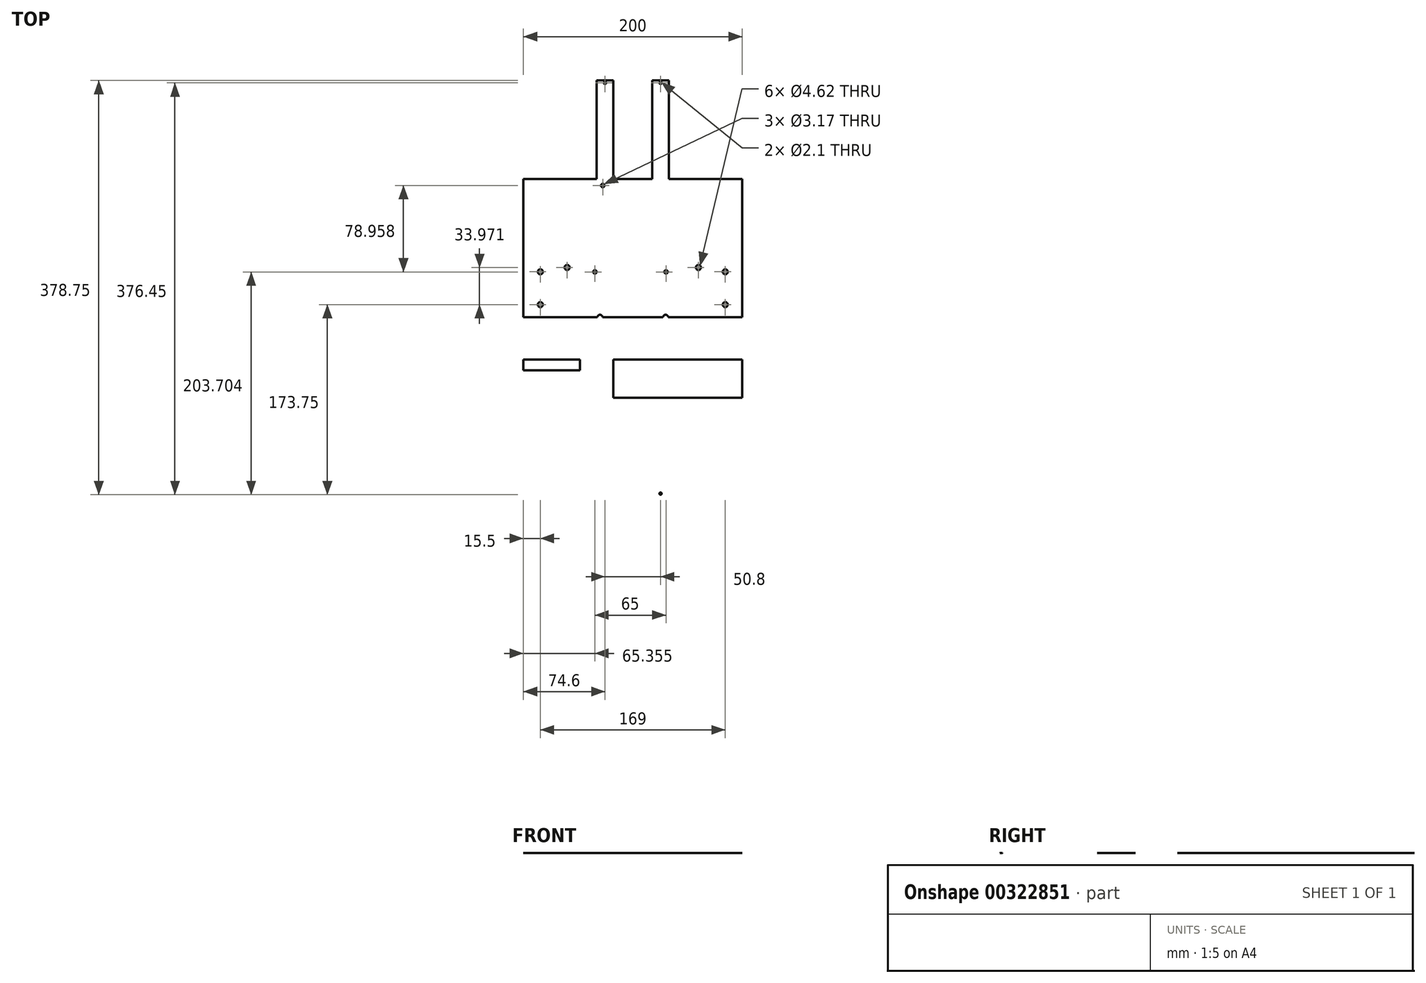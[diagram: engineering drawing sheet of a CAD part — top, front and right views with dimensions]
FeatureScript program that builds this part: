
annotation { "Feature Type Name" : "Feature", "Feature Type Description" : "" }
export const myFeature = defineFeature(function(context is Context, id is Id, definition is map)
    precondition{}
    {
        {
            var Q0;
            Q0=qCreatedBy(makeId("Top.planeOp"),FACE);
            var sketch = newSketch(context, id + "F0", { "sketchPlane" : qUnion([Q0])});
            skLineSegment(sketch, "E0.bottom", {"start": v(100, -100) * mm, "end": v(-100, -100) * mm});
            skLineSegment(sketch, "E0.top", {"start": v(100, 100) * mm, "end": v(-100, 100) * mm});
            skLineSegment(sketch, "E0.left", {"start": v(100, -100) * mm, "end": v(100, 100) * mm});
            skLineSegment(sketch, "E0.right", {"start": v(-100, -100) * mm, "end": v(-100, 100) * mm});
            skPoint(sketch, "E0.middle", {"position": v(0, 0) * mm});
            skLineSegment(sketch, "E1", {"start": v(-100, -100) * mm, "end": v(-100, -65.07) * mm});
            skLineSegment(sketch, "E2", {"start": v(-100, -65.07) * mm, "end": v(100, -65.07) * mm});
            skLineSegment(sketch, "E3", {"start": v(100, -65.07) * mm, "end": v(-100, -65.08) * mm});
            skLineSegment(sketch, "E4", {"start": v(-100, 100) * mm, "end": v(-100, 65.07) * mm});
            skLineSegment(sketch, "E5", {"start": v(-100, 65.07) * mm, "end": v(-42.4, 65.07) * mm});
            skLineSegment(sketch, "E6", {"start": v(100, 65.08) * mm, "end": v(42.4, 65.08) * mm});
            skLineSegment(sketch, "E7", {"start": v(-100, -65.07) * mm, "end": v(-100, -55.08) * mm});
            skLineSegment(sketch, "E8.bottom", {"start": v(-100, -55.08) * mm, "end": v(-48.2, -55.08) * mm});
            skLineSegment(sketch, "E8.top", {"start": v(-100, -75.08) * mm, "end": v(-48.2, -75.08) * mm});
            skLineSegment(sketch, "E8.left", {"start": v(-100, -55.08) * mm, "end": v(-100, -75.08) * mm});
            skLineSegment(sketch, "E8.right", {"start": v(-48.2, -55.08) * mm, "end": v(-48.2, -75.08) * mm});
            skPoint(sketch, "E9.startSnap0", {"position": v(-100, 0) * mm});
            skLineSegment(sketch, "E10.MirrorCS", {"start": v(48.2, -55.08) * mm, "end": v(48.2, -75.08) * mm});
            skLineSegment(sketch, "E11.MirrorCS", {"start": v(100, -75.08) * mm, "end": v(48.2, -75.08) * mm});
            skLineSegment(sketch, "E12.MirrorCS", {"start": v(100, -55.08) * mm, "end": v(48.2, -55.08) * mm});
            skLineSegment(sketch, "E13.MirrorCS", {"start": v(100, 55.08) * mm, "end": v(48.2, 55.08) * mm});
            skLineSegment(sketch, "E14.MirrorCS", {"start": v(48.2, 55.08) * mm, "end": v(48.2, 75.08) * mm});
            skLineSegment(sketch, "E15.MirrorCS", {"start": v(100, 75.08) * mm, "end": v(48.2, 75.08) * mm});
            skLineSegment(sketch, "E16.MirrorCS", {"start": v(-48.2, 55.07) * mm, "end": v(-48.2, 75.07) * mm});
            skLineSegment(sketch, "E17.MirrorCS", {"start": v(-100, 75.07) * mm, "end": v(-48.2, 75.07) * mm});
            skLineSegment(sketch, "E18.MirrorCS", {"start": v(-100, 55.07) * mm, "end": v(-48.2, 55.07) * mm});
            skLineSegment(sketch, "E19.bottom", {"start": v(-100, -55.08) * mm, "end": v(100, -55.08) * mm});
            skLineSegment(sketch, "E19.top", {"start": v(-100, -26.57) * mm, "end": v(100, -26.57) * mm});
            skLineSegment(sketch, "E19.left", {"start": v(-100, -55.08) * mm, "end": v(-100, -26.57) * mm});
            skLineSegment(sketch, "E19.right", {"start": v(100, -55.08) * mm, "end": v(100, -26.57) * mm});
            skLineSegment(sketch, "E20", {"start": v(0, -26.57) * mm, "end": v(30, -26.57) * mm});
            skLineSegment(sketch, "E21", {"start": v(30, -26.57) * mm, "end": v(-30, -26.57) * mm});
            skCircle(sketch, "E22", {"center": v(-30, -26.57) * mm, "radius": 2.31 * mm});
            skCircle(sketch, "E23.MirrorC", {"center": v(30, -26.57) * mm, "radius": 2.31 * mm});
            skLineSegment(sketch, "E24", {"start": v(0, 100) * mm, "end": v(42.4, 100) * mm});
            skLineSegment(sketch, "E25.bottom", {"start": v(42.4, 100) * mm, "end": v(-42.4, 100) * mm});
            skLineSegment(sketch, "E25.top", {"start": v(42.4, 9.75) * mm, "end": v(-42.4, 9.75) * mm});
            skLineSegment(sketch, "E25.left", {"start": v(42.4, 100) * mm, "end": v(42.4, 9.75) * mm});
            skLineSegment(sketch, "E25.right", {"start": v(-42.4, 100) * mm, "end": v(-42.4, 9.75) * mm});
            skPoint(sketch, "E26.start.orphan", {"position": v(0, 18.97) * mm});
            skPoint(sketch, "E27.orphan", {"position": v(-14.32, 0) * mm});
            skLineSegment(sketch, "E28", {"start": v(42.4, 18.97) * mm, "end": v(60, 18.97) * mm});
            skLineSegment(sketch, "E29", {"start": v(60, 18.97) * mm, "end": v(57.69, 18.97) * mm});
            skLineSegment(sketch, "E30", {"start": v(-57.69, 18.97) * mm, "end": v(-60, 18.97) * mm});
            skCircle(sketch, "E31", {"center": v(-60, 18.97) * mm, "radius": 2.31 * mm});
            skCircle(sketch, "E32", {"center": v(60, 18.97) * mm, "radius": 2.31 * mm});
            skLineSegment(sketch, "E33", {"start": v(42.4, 9.75) * mm, "end": v(30.36, 9.75) * mm});
            skLineSegment(sketch, "E34", {"start": v(30.36, 9.75) * mm, "end": v(30.36, 14.95) * mm});
            skCircle(sketch, "E35", {"center": v(30.36, 14.95) * mm, "radius": 1.59 * mm});
            skLineSegment(sketch, "E36", {"start": v(30.36, 14.95) * mm, "end": v(28.77, 14.95) * mm});
            skCircle(sketch, "E37", {"center": v(-34.64, 14.95) * mm, "radius": 1.59 * mm});
            skLineSegment(sketch, "E38", {"start": v(-34.64, 14.95) * mm, "end": v(-27.46, 14.95) * mm});
            skLineSegment(sketch, "E39", {"start": v(-27.46, 92.32) * mm, "end": v(-27.46, 100) * mm});
            skLineSegment(sketch, "E40", {"start": v(-27.46, 100) * mm, "end": v(-27.46, 93.91) * mm});
            skCircle(sketch, "E41", {"center": v(-27.46, 93.91) * mm, "radius": 1.59 * mm});
            skLineSegment(sketch, "E42.trimOffspring", {"start": v(-27.46, 14.95) * mm, "end": v(-34.64, 14.95) * mm});
            skLineSegment(sketch, "E43.trimOffspring", {"start": v(-27.46, 65.07) * mm, "end": v(-42.4, 65.07) * mm});
            skLineSegment(sketch, "E44.trimOffspring", {"start": v(42.4, 65.08) * mm, "end": v(100, 65.08) * mm});
            skLineSegment(sketch, "E45", {"start": v(-100, 0) * mm, "end": v(-84.5, 0) * mm});
            skLineSegment(sketch, "E46", {"start": v(-84.5, 0) * mm, "end": v(-84.5, 15) * mm});
            skLineSegment(sketch, "E47", {"start": v(-84.5, 15) * mm, "end": v(-84.5, -15) * mm});
            skPoint(sketch, "E47.endSnap0", {"position": v(-84.5, 7.5) * mm});
            skCircle(sketch, "E48", {"center": v(-84.5, -15) * mm, "radius": 2.31 * mm});
            skCircle(sketch, "E49", {"center": v(-84.5, 15) * mm, "radius": 2.31 * mm});
            skLineSegment(sketch, "E50", {"start": v(0, -26.57) * mm, "end": v(0, -10.45) * mm});
            skCircle(sketch, "E51.MirrorC", {"center": v(84.5, -15) * mm, "radius": 2.31 * mm});
            skCircle(sketch, "E52.MirrorC", {"center": v(84.5, 15) * mm, "radius": 2.31 * mm});
            skLineSegment(sketch, "E53.left", {"start": v(33.02, -65.07) * mm, "end": v(33.02, -60) * mm});
            skLineSegment(sketch, "E53.right", {"start": v(-33.02, -65.07) * mm, "end": v(-33.02, -60) * mm});
            skPoint(sketch, "E53.middle", {"position": v(0, -100) * mm});
            skLineSegment(sketch, "E54.left", {"start": v(17.78, -65.07) * mm, "end": v(17.78, -60) * mm});
            skLineSegment(sketch, "E54.right", {"start": v(-17.78, -65.07) * mm, "end": v(-17.78, -60) * mm});
            skCircle(sketch, "E55.MirrorC", {"center": v(-25.4, -137.7) * mm, "radius": 1.05 * mm});
            skLineSegment(sketch, "E56", {"start": v(100, 0) * mm, "end": v(0, 0) * mm});
            skLineSegment(sketch, "E57.MirrorCS", {"start": v(33.02, 140) * mm, "end": v(33.02, 60) * mm});
            skLineSegment(sketch, "E58.MirrorCS", {"start": v(17.78, 140) * mm, "end": v(17.78, 60) * mm});
            skLineSegment(sketch, "E59.MirrorCS", {"start": v(-17.78, 140) * mm, "end": v(-17.78, 60) * mm});
            skLineSegment(sketch, "E60.MirrorCS", {"start": v(-33.02, 140) * mm, "end": v(-33.02, 60) * mm});
            skLineSegment(sketch, "E61", {"start": v(0, 0) * mm, "end": v(0, -10.45) * mm});
            skLineSegment(sketch, "E62", {"start": v(33.02, 140) * mm, "end": v(33.02, 190) * mm});
            skLineSegment(sketch, "E63", {"start": v(33.02, 190) * mm, "end": v(17.78, 190) * mm});
            skLineSegment(sketch, "E64", {"start": v(17.78, 190) * mm, "end": v(17.78, 140) * mm});
            skLineSegment(sketch, "E65", {"start": v(-17.78, 140) * mm, "end": v(-17.78, 190) * mm});
            skLineSegment(sketch, "E66", {"start": v(-17.78, 190) * mm, "end": v(-33.02, 190) * mm});
            skLineSegment(sketch, "E67", {"start": v(-33.02, 190) * mm, "end": v(-33.02, 140) * mm});
            skPoint(sketch, "E68.MirrorCS.start.orphan", {"position": v(33.02, 140) * mm});
            skLineSegment(sketch, "E69", {"start": v(25.4, 190) * mm, "end": v(25.4, 187.7) * mm});
            skCircle(sketch, "E70", {"center": v(25.4, 187.7) * mm, "radius": 1.05 * mm});
            skPoint(sketch, "E71.MirrorC.center.orphan", {"position": v(25.4, 137.7) * mm});
            skLineSegment(sketch, "E72", {"start": v(-25.4, 190) * mm, "end": v(-25.4, 187.7) * mm});
            skCircle(sketch, "E73", {"center": v(-25.4, 187.7) * mm, "radius": 1.05 * mm});
            skPoint(sketch, "E74.orphan", {"position": v(-33.02, -140) * mm});
            skPoint(sketch, "E75.orphan", {"position": v(-17.78, -140) * mm});
            skPoint(sketch, "E53.bottom.start.orphan", {"position": v(25.4, -140) * mm});
            skPoint(sketch, "E76.orphan", {"position": v(33.02, -140) * mm});
            skPoint(sketch, "E77.start.orphan", {"position": v(17.78, -140) * mm});
            skLineSegment(sketch, "E78.MirrorCS", {"start": v(-27.46, -92.32) * mm, "end": v(-27.46, -100) * mm});
            skCircle(sketch, "E79.MirrorC", {"center": v(-27.46, -93.91) * mm, "radius": 1.59 * mm});
            skLineSegment(sketch, "E80.MirrorCS", {"start": v(-27.46, -100) * mm, "end": v(-27.46, -93.91) * mm});
            skLineSegment(sketch, "E81.MirrorCS", {"start": v(-17.78, -190) * mm, "end": v(-33.02, -190) * mm});
            skCircle(sketch, "E82.MirrorC", {"center": v(-25.4, -187.7) * mm, "radius": 1.05 * mm});
            skLineSegment(sketch, "E83.MirrorCS", {"start": v(-25.4, -190) * mm, "end": v(-25.4, -187.7) * mm});
            skCircle(sketch, "E84.MirrorC", {"center": v(25.4, -187.7) * mm, "radius": 1.05 * mm});
            skLineSegment(sketch, "E85.MirrorCS", {"start": v(33.02, -190) * mm, "end": v(17.78, -190) * mm});
            skLineSegment(sketch, "E86.MirrorCS", {"start": v(25.4, -190) * mm, "end": v(25.4, -187.7) * mm});
            skLineSegment(sketch, "E87.MirrorCS", {"start": v(42.4, -100) * mm, "end": v(-42.4, -100) * mm});
            skLineSegment(sketch, "E88.MirrorCS", {"start": v(0, -100) * mm, "end": v(42.4, -100) * mm});
            skLineSegment(sketch, "E89.MirrorCS", {"start": v(17.78, -190) * mm, "end": v(17.78, -140) * mm});
            skPoint(sketch, "E90.MirrorP", {"position": v(25.4, -137.7) * mm});
            skLineSegment(sketch, "E91.MirrorCS", {"start": v(-17.78, -140) * mm, "end": v(-17.78, -190) * mm});
            skLineSegment(sketch, "E92.MirrorCS", {"start": v(33.02, -140) * mm, "end": v(33.02, -190) * mm});
            skLineSegment(sketch, "E93.MirrorCS", {"start": v(-33.02, -190) * mm, "end": v(-33.02, -140) * mm});
            skLineSegment(sketch, "E94.MirrorCS", {"start": v(-33.02, -140) * mm, "end": v(-33.02, -60) * mm});
            skLineSegment(sketch, "E95.MirrorCS", {"start": v(-17.78, -140) * mm, "end": v(-17.78, -60) * mm});
            skLineSegment(sketch, "E96.MirrorCS", {"start": v(17.78, -140) * mm, "end": v(17.78, -60) * mm});
            skLineSegment(sketch, "E97.MirrorCS", {"start": v(33.02, -140) * mm, "end": v(33.02, -60) * mm});
            skSolve(sketch);
        }
        {
            var Q0;
            {var subQ3=sQuery(id+"F0.wireOp",EDGE,"E11.MirrorCS");Q0=makeQuery(id+"F0.imprint","IMPRINT",FACE,{"disambiguationData":[TD([[makeQuery(id+"F0.imprint","IMPRINT",EDGE,{"derivedFrom":subQ3}),-1.0]])]});}
            var Q1;
            {var subQ0=sQuery(id+"F0.wireOp",EDGE,"E13.MirrorCS");Q1=makeQuery(id+"F0.imprint","IMPRINT",FACE,{"disambiguationData":[TD([[makeQuery(id+"F0.imprint","IMPRINT",EDGE,{"derivedFrom":subQ0}),-1.0]])]});}
            var Q2;
            {var subQ0=sQuery(id+"F0.wireOp",EDGE,"E15.MirrorCS");Q2=makeQuery(id+"F0.imprint","IMPRINT",FACE,{"disambiguationData":[TD([[makeQuery(id+"F0.imprint","IMPRINT",EDGE,{"derivedFrom":subQ0}),1.0]])]});}
            var Q3;
            {var subQ3=sQuery(id+"F0.wireOp",EDGE,"E18.MirrorCS");Q3=makeQuery(id+"F0.imprint","IMPRINT",FACE,{"disambiguationData":[TD([[makeQuery(id+"F0.imprint","IMPRINT",EDGE,{"derivedFrom":subQ3}),1.0]])]});}
            var Q4;
            {var subQ5=sQuery(id+"F0.wireOp",EDGE,"E8.top");Q4=makeQuery(id+"F0.imprint","IMPRINT",FACE,{"disambiguationData":[TD([[makeQuery(id+"F0.imprint","IMPRINT",EDGE,{"derivedFrom":subQ5}),1.0]])]});}
            var Q5;
            {var subQ3=sQuery(id+"F0.wireOp",EDGE,"E17.MirrorCS");Q5=makeQuery(id+"F0.imprint","IMPRINT",FACE,{"disambiguationData":[TD([[makeQuery(id+"F0.imprint","IMPRINT",EDGE,{"derivedFrom":subQ3}),-1.0]])]});}
            var Q6;
            {var subQ3=sQuery(id+"F0.wireOp",EDGE,"E60.MirrorCS");var subQ5=sQuery(id+"F0.wireOp",EDGE,"E43.trimOffspring");var subQ7=makeQuery(id+"F0.imprint","INTERSECT",VERTEX,{"derivedFrom":[subQ5,subQ3]});Q6=makeQuery(id+"F0.imprint","IMPRINT",FACE,{"disambiguationData":[TD([[makeQuery(id+"F0.imprint","IMPRINT",EDGE,{"disambiguationData":[TD([[subQ7,1.0]])],"derivedFrom":subQ3}),-1.0]])]});}
            var Q7;
            {var subQ0=sQuery(id+"F0.wireOp",EDGE,"E11.MirrorCS");Q7=makeQuery(id+"F0.imprint","IMPRINT",FACE,{"disambiguationData":[TD([[makeQuery(id+"F0.imprint","IMPRINT",EDGE,{"derivedFrom":subQ0}),1.0]])]});}
            var Q8;
            Q8=makeQuery(id+"F0.imprint","IMPRINT",FACE,{"disambiguationData":[TD([[makeQuery(id+"F0.imprint","IMPRINT",EDGE,{"derivedFrom":sQuery(id+"F0.wireOp",EDGE,"eKkkPPQE-iV3J-UeWj-UhbM-f08VdtV66dPE")}),-1.0]])]});
            var Q9;
            {var subQ1=sQuery(id+"F0.wireOp",EDGE,"E53.bottom");Q9=makeQuery(id+"F0.imprint","IMPRINT",FACE,{"disambiguationData":[TD([[makeQuery(id+"F0.imprint","IMPRINT",EDGE,{"derivedFrom":subQ1}),-1.0]])]});}
            var Q10;
            {var subQ1=sQuery(id+"F0.wireOp",EDGE,"E1");Q10=makeQuery(id+"F0.imprint","IMPRINT",FACE,{"disambiguationData":[TD([[makeQuery(id+"F0.imprint","IMPRINT",EDGE,{"derivedFrom":subQ1}),-1.0]])]});}
            var Q11;
            {var subQ0=sQuery(id+"F0.wireOp",EDGE,"E15.MirrorCS");Q11=makeQuery(id+"F0.imprint","IMPRINT",FACE,{"disambiguationData":[TD([[makeQuery(id+"F0.imprint","IMPRINT",EDGE,{"derivedFrom":subQ0}),-1.0]])]});}
            var Q12;
            {var subQ0=sQuery(id+"F0.wireOp",EDGE,"E17.MirrorCS");Q12=makeQuery(id+"F0.imprint","IMPRINT",FACE,{"disambiguationData":[TD([[makeQuery(id+"F0.imprint","IMPRINT",EDGE,{"derivedFrom":subQ0}),1.0]])]});}
            var Q13;
            {var subQ0=sQuery(id+"F0.wireOp",EDGE,"E3");var subQ1=sQuery(id+"F0.wireOp",EDGE,"E0.left");var subQ2=makeQuery(id+"F0.imprint","INTERSECT",VERTEX,{"derivedFrom":[subQ1,subQ0]});Q13=makeQuery(id+"F0.imprint","IMPRINT",FACE,{"disambiguationData":[TD([[makeQuery(id+"F0.imprint","IMPRINT",EDGE,{"disambiguationData":[TD([[subQ2,-1.0]])],"derivedFrom":subQ0}),-1.0]])]});}
            var Q14;
            {var subQ0=sQuery(id+"F0.wireOp",EDGE,"E8.left");var subQ1=sQuery(id+"F0.wireOp",EDGE,"E3");var subQ2=makeQuery(id+"F0.imprint","INTERSECT",VERTEX,{"derivedFrom":[subQ1,subQ0]});Q14=makeQuery(id+"F0.imprint","IMPRINT",FACE,{"disambiguationData":[TD([[makeQuery(id+"F0.imprint","IMPRINT",EDGE,{"disambiguationData":[TD([[subQ2,1.0]])],"derivedFrom":subQ1}),-1.0]])]});}
            var Q15;
            Q15=makeQuery(id+"F0.imprint","IMPRINT",FACE,{"disambiguationData":[TD([[makeQuery(id+"F0.imprint","IMPRINT",EDGE,{"derivedFrom":sQuery(id+"F0.wireOp",EDGE,"E71.MirrorC")}),1.0]])]});
            var Q16;
            Q16=makeQuery(id+"F0.imprint","IMPRINT",FACE,{"disambiguationData":[TD([[makeQuery(id+"F0.imprint","IMPRINT",EDGE,{"derivedFrom":sQuery(id+"F0.wireOp",EDGE,"d2df25b0-5026-4a67-b89d-bc6038fde6b30.MirrorC")}),-1.0]])]});
            var Q17;
            {var subQ0=sQuery(id+"F0.wireOp",EDGE,"E53.left");var subQ1=sQuery(id+"F0.wireOp",EDGE,"E0.bottom");var subQ2=makeQuery(id+"F0.imprint","INTERSECT",VERTEX,{"derivedFrom":[subQ1,subQ0]});Q17=makeQuery(id+"F0.imprint","IMPRINT",FACE,{"disambiguationData":[TD([[makeQuery(id+"F0.imprint","IMPRINT",EDGE,{"disambiguationData":[TD([[subQ2,-1.0]])],"derivedFrom":subQ1}),-1.0]])]});}
            var Q18;
            {var subQ0=sQuery(id+"F0.wireOp",EDGE,"E53.right");var subQ1=sQuery(id+"F0.wireOp",EDGE,"E0.bottom");var subQ2=makeQuery(id+"F0.imprint","INTERSECT",VERTEX,{"derivedFrom":[subQ1,subQ0]});Q18=makeQuery(id+"F0.imprint","IMPRINT",FACE,{"disambiguationData":[TD([[makeQuery(id+"F0.imprint","IMPRINT",EDGE,{"disambiguationData":[TD([[subQ2,1.0]])],"derivedFrom":subQ1}),-1.0]])]});}
            var Q19;
            {var subQ5=sQuery(id+"F0.wireOp",EDGE,"E19.left");Q19=makeQuery(id+"F0.imprint","IMPRINT",FACE,{"disambiguationData":[TD([[makeQuery(id+"F0.imprint","IMPRINT",EDGE,{"derivedFrom":subQ5}),-1.0]])]});}
            var Q20;
            {var subQ6=sQuery(id+"F0.wireOp",EDGE,"E25.top");Q20=makeQuery(id+"F0.imprint","IMPRINT",FACE,{"disambiguationData":[TD([[makeQuery(id+"F0.imprint","IMPRINT",EDGE,{"derivedFrom":subQ6}),-1.0]])]});}
            var Q21;
            {var subQ22=sQuery(id+"F0.wireOp",EDGE,"E13.MirrorCS");Q21=makeQuery(id+"F0.imprint","IMPRINT",FACE,{"disambiguationData":[TD([[makeQuery(id+"F0.imprint","IMPRINT",EDGE,{"derivedFrom":subQ22}),1.0]])]});}
            var Q22;
            {var subQ14=sQuery(id+"F0.wireOp",EDGE,"E54.top");Q22=makeQuery(id+"F0.imprint","IMPRINT",FACE,{"disambiguationData":[TD([[makeQuery(id+"F0.imprint","IMPRINT",EDGE,{"derivedFrom":subQ14}),-1.0]])]});}
            var Q23;
            {var subQ0=sQuery(id+"F0.wireOp",EDGE,"E54.left");var subQ1=sQuery(id+"F0.wireOp",EDGE,"E0.bottom");var subQ2=makeQuery(id+"F0.imprint","INTERSECT",VERTEX,{"derivedFrom":[subQ1,subQ0]});Q23=makeQuery(id+"F0.imprint","IMPRINT",FACE,{"disambiguationData":[TD([[makeQuery(id+"F0.imprint","IMPRINT",EDGE,{"disambiguationData":[TD([[subQ2,-1.0]])],"derivedFrom":subQ1}),-1.0]])]});}
            var Q24;
            {var subQ5=sQuery(id+"F0.wireOp",EDGE,"E54.top");Q24=makeQuery(id+"F0.imprint","IMPRINT",FACE,{"disambiguationData":[TD([[makeQuery(id+"F0.imprint","IMPRINT",EDGE,{"derivedFrom":subQ5}),1.0]])]});}
            var Q25;
            {var subQ0=sQuery(id+"F0.wireOp",EDGE,"E53.left");var subQ1=sQuery(id+"F0.wireOp",EDGE,"E3");var subQ2=makeQuery(id+"F0.imprint","INTERSECT",VERTEX,{"derivedFrom":[subQ1,subQ0]});Q25=makeQuery(id+"F0.imprint","IMPRINT",FACE,{"disambiguationData":[TD([[makeQuery(id+"F0.imprint","IMPRINT",EDGE,{"disambiguationData":[TD([[subQ2,-1.0]])],"derivedFrom":subQ1}),-1.0]])]});}
            var Q26;
            {var subQ0=sQuery(id+"F0.wireOp",EDGE,"E54.right");var subQ1=sQuery(id+"F0.wireOp",EDGE,"E3");var subQ2=makeQuery(id+"F0.imprint","INTERSECT",VERTEX,{"derivedFrom":[subQ1,subQ0]});Q26=makeQuery(id+"F0.imprint","IMPRINT",FACE,{"disambiguationData":[TD([[makeQuery(id+"F0.imprint","IMPRINT",EDGE,{"disambiguationData":[TD([[subQ2,-1.0]])],"derivedFrom":subQ1}),-1.0]])]});}
            var Q27;
            {var subQ5=sQuery(id+"F0.wireOp",EDGE,"E50");Q27=makeQuery(id+"F0.imprint","IMPRINT",FACE,{"disambiguationData":[TD([[makeQuery(id+"F0.imprint","IMPRINT",EDGE,{"derivedFrom":subQ5}),-1.0]])]});}
            var Q28;
            Q28=makeQuery(id+"F0.imprint","IMPRINT",FACE,{"disambiguationData":[TD([[makeQuery(id+"F0.imprint","IMPRINT",EDGE,{"derivedFrom":sQuery(id+"F0.wireOp",EDGE,"E55.MirrorC")}),1.0]])]});
            var Q29;
            {var subQ6=sQuery(id+"F0.wireOp",EDGE,"E87.MirrorCS");var subQ8=makeQuery(id+"F0.imprint","IMPRINT",VERTEX,{"derivedFrom":subQ6});Q29=makeQuery(id+"F0.imprint","IMPRINT",FACE,{"disambiguationData":[TD([[makeQuery(id+"F0.imprint","IMPRINT",EDGE,{"disambiguationData":[TD([[subQ8,1.0]])],"derivedFrom":subQ6}),-1.0]])]});}
            var Q30;
            {var subQ5=sQuery(id+"F0.wireOp",EDGE,"E3");var subQ7=sQuery(id+"F0.wireOp",EDGE,"E96.MirrorCS");var subQ9=makeQuery(id+"F0.imprint","INTERSECT",VERTEX,{"derivedFrom":[subQ5,subQ7]});Q30=makeQuery(id+"F0.imprint","IMPRINT",FACE,{"disambiguationData":[TD([[makeQuery(id+"F0.imprint","IMPRINT",EDGE,{"disambiguationData":[TD([[subQ9,-1.0]])],"derivedFrom":subQ5}),1.0]])]});}
            var Q31;
            {var subQ0=sQuery(id+"F0.wireOp",EDGE,"E97.MirrorCS");var subQ1=sQuery(id+"F0.wireOp",EDGE,"E3");var subQ2=makeQuery(id+"F0.imprint","INTERSECT",VERTEX,{"derivedFrom":[subQ1,subQ0]});Q31=makeQuery(id+"F0.imprint","IMPRINT",FACE,{"disambiguationData":[TD([[makeQuery(id+"F0.imprint","IMPRINT",EDGE,{"disambiguationData":[TD([[subQ2,-1.0]])],"derivedFrom":subQ1}),1.0]])]});}
            var Q32;
            Q32=makeQuery(id+"F0.imprint","IMPRINT",FACE,{"disambiguationData":[TD([[makeQuery(id+"F0.imprint","IMPRINT",EDGE,{"derivedFrom":sQuery(id+"F0.wireOp",EDGE,"E84.MirrorC")}),1.0]])]});
            var Q33;
            {var subQ0=sQuery(id+"F0.wireOp",EDGE,"E62");Q33=makeQuery(id+"F0.imprint","IMPRINT",FACE,{"disambiguationData":[TD([[makeQuery(id+"F0.imprint","IMPRINT",EDGE,{"derivedFrom":subQ0}),1.0]])]});}
            var Q34;
            {var subQ5=sQuery(id+"F0.wireOp",EDGE,"E65");Q34=makeQuery(id+"F0.imprint","IMPRINT",FACE,{"disambiguationData":[TD([[makeQuery(id+"F0.imprint","IMPRINT",EDGE,{"derivedFrom":subQ5}),1.0]])]});}
            var Q35;
            Q35=makeQuery(id+"F0.imprint","IMPRINT",FACE,{"disambiguationData":[TD([[makeQuery(id+"F0.imprint","IMPRINT",EDGE,{"derivedFrom":sQuery(id+"F0.wireOp",EDGE,"E55.MirrorC")}),-1.0]])]});
            extrude(context, id + "F1", {"entities" : qUnion([Q0, Q1, Q2, Q3, Q4, Q5, Q6, Q7, Q8, Q9, Q10, Q11, Q12, Q13, Q14, Q15, Q16, Q17, Q18, Q19, Q20, Q21, Q22, Q23, Q24, Q25, Q26, Q27, Q28, Q29, Q30, Q31, Q32, Q33, Q34, Q35]), "depth" : 1 / 203.2 * mm});
        }
        {
            var Q0;
            Q0=makeQuery(id+"F1.opExtrude","SWEPT_FACE",FACE,{"disambiguationData":[OSD([sQuery(id+"F0.wireOp",EDGE,"E85.MirrorCS")])]});
            var Q1;
            Q1=makeQuery(id+"F1.opExtrude","SWEPT_FACE",FACE,{"disambiguationData":[OSD([sQuery(id+"F0.wireOp",EDGE,"E81.MirrorCS")])]});
            extrude(context, id + "F2", {"entities" : qUnion([Q0, Q1]), "operationType" : NewBodyOperationType.REMOVE, "oppositeDirection" : true, "depth" : 90 * mm});
        }
    });
